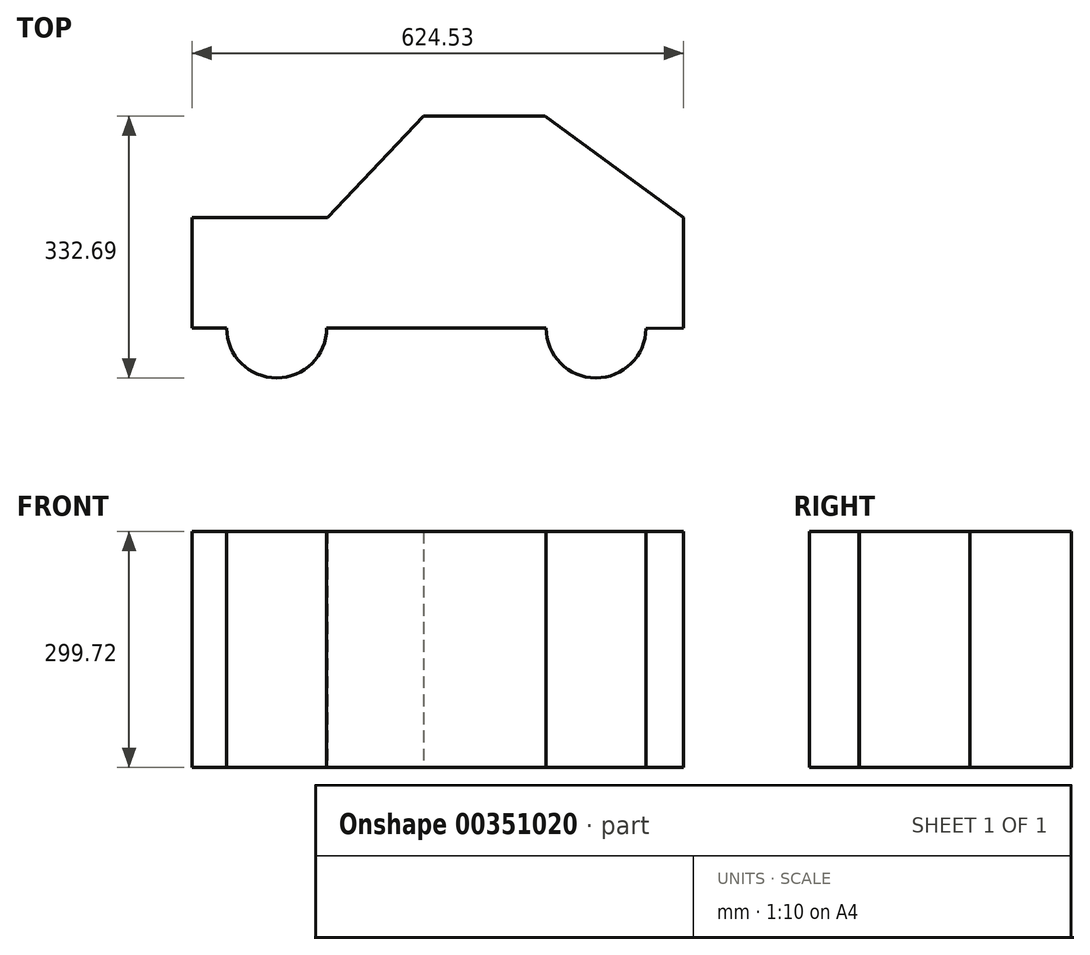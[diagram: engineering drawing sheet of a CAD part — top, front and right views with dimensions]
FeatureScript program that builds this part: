
annotation { "Feature Type Name" : "Feature", "Feature Type Description" : "" }
export const myFeature = defineFeature(function(context is Context, id is Id, definition is map)
    precondition{}
    {
        {
            var Q0;
            Q0=qCreatedBy(makeId("Top.planeOp"),FACE);
            var sketch = newSketch(context, id + "F0", { "sketchPlane" : qUnion([Q0])});
            skLineSegment(sketch, "E0.left", {"start": v(-283.67, 50.26) * mm, "end": v(-283.67, -89.72) * mm});
            skLineSegment(sketch, "E0.right", {"start": v(340.86, 50.26) * mm, "end": v(340.86, -89.72) * mm});
            skLineSegment(sketch, "E1", {"start": v(-111.38, 50.26) * mm, "end": v(10.65, 179.47) * mm});
            skLineSegment(sketch, "E2", {"start": v(10.65, 179.47) * mm, "end": v(164.99, 179.47) * mm});
            skLineSegment(sketch, "E3", {"start": v(164.99, 179.47) * mm, "end": v(340.86, 50.26) * mm});
            skLineSegment(sketch, "E4", {"start": v(-283.67, 50.26) * mm, "end": v(-111.38, 50.26) * mm});
            skCircle(sketch, "E5", {"center": v(-176, -89.72) * mm, "radius": 63.5 * mm});
            skCircle(sketch, "E6", {"center": v(229.6, -89.72) * mm, "radius": 63.5 * mm});
            skLineSegment(sketch, "E7", {"start": v(-621.49, -185.39) * mm, "end": v(616.15, -185.39) * mm});
            skLineSegment(sketch, "E8", {"start": v(-283.67, -89.72) * mm, "end": v(-239.5, -89.72) * mm});
            skLineSegment(sketch, "E9", {"start": v(-112.5, -89.72) * mm, "end": v(166.1, -89.72) * mm});
            skLineSegment(sketch, "E10", {"start": v(293.1, -90.3) * mm, "end": v(340.86, -89.72) * mm});
            skSolve(sketch);
        }
        {
            var Q0;
            Q0=makeQuery(id+"F0.imprint","IMPRINT",FACE,{"disambiguationData":[TD([[makeQuery(id+"F0.imprint","IMPRINT",EDGE,{"derivedFrom":sQuery(id+"F0.wireOp",EDGE,"E0.left")}),1.0]])]});
            var Q1;
            {var subQ0=sQuery(id+"F0.wireOp",EDGE,"E5");var subQ1=makeQuery(id+"F0.imprint","INTERSECT",VERTEX,{"derivedFrom":[subQ0,sQuery(id+"F0.wireOp",EDGE,"E8")]});Q1=makeQuery(id+"F0.imprint","IMPRINT",FACE,{"disambiguationData":[TD([[makeQuery(id+"F0.imprint","IMPRINT",EDGE,{"disambiguationData":[TD([[subQ1,1.0]])],"derivedFrom":subQ0}),1.0]])]});}
            var Q2;
            {var subQ0=sQuery(id+"F0.wireOp",EDGE,"E6");var subQ1=makeQuery(id+"F0.imprint","INTERSECT",VERTEX,{"derivedFrom":[subQ0,sQuery(id+"F0.wireOp",EDGE,"E9")]});Q2=makeQuery(id+"F0.imprint","IMPRINT",FACE,{"disambiguationData":[TD([[makeQuery(id+"F0.imprint","IMPRINT",EDGE,{"disambiguationData":[TD([[subQ1,-1.0]])],"derivedFrom":subQ0}),1.0]])]});}
            extrude(context, id + "F1", {"entities" : qUnion([Q0, Q1, Q2]), "depth" : 299.72 * mm});
        }
    });
